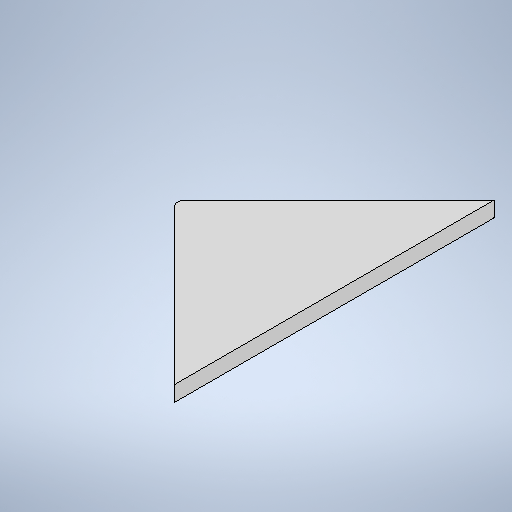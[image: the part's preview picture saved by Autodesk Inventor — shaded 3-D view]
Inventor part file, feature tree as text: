
AUTODESK INVENTOR PART (.ipt)
format: ipt  version: 2025 (Build 290162010, 162A)  size: 258,560 bytes
history: native  units: mm
features: sketch x2, sheet_metal_op x1, chamfer x1, extrude x1, other x1
ambient origin geometry x8: Origin, YZ Plane, XZ Plane, XY Plane, X Axis, Y Axis, Z Axis, Center Point
bodies: Solid1 (feature_tree)
feature tree (6):
  sheet_metal_op  "Face1"
  chamfer  "Corner Round2"
  extrude  "Extrusion1"  Depth=42.0mm
  sketch  "Sketch1"  dims[d0=41.0mm d1=42.0mm]
  other  "Plate1"
  sketch  "Sketch2"  dims[d2=2.0mm d4=62.0mm d6=1.0mm d7=0.0mm d8=0.0mm]
